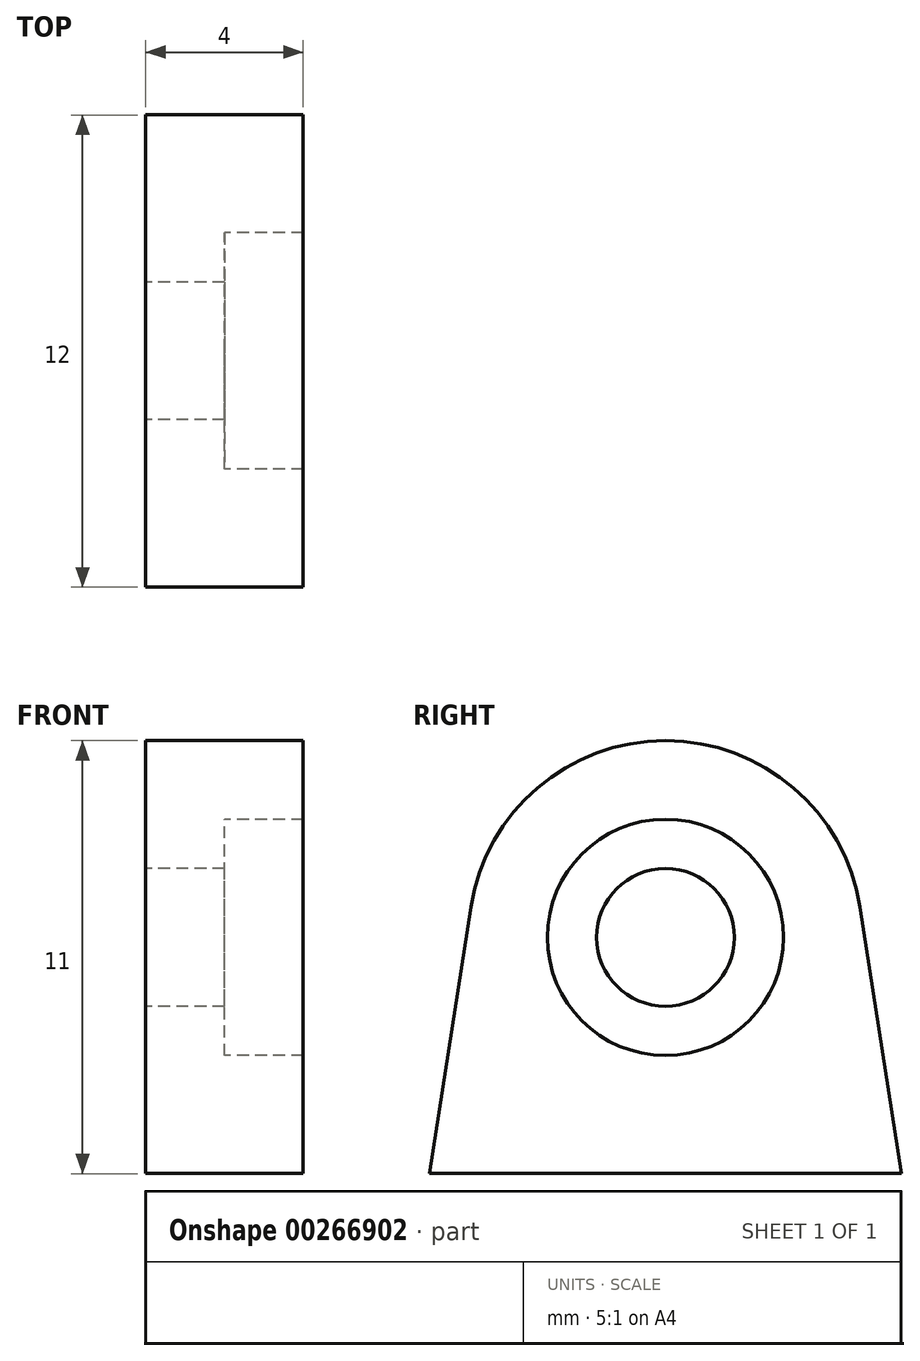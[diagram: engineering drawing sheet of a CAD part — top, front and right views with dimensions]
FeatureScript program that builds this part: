
annotation { "Feature Type Name" : "Feature", "Feature Type Description" : "" }
export const myFeature = defineFeature(function(context is Context, id is Id, definition is map)
    precondition{}
    {
        {
            var Q0;
            Q0=qCreatedBy(makeId("Right.planeOp"),FACE);
            var sketch = newSketch(context, id + "F0", { "sketchPlane" : qUnion([Q0])});
            skCircle(sketch, "E0", {"center": v(-26.77, 32.62) * mm, "radius": 5 * mm});
            skLineSegment(sketch, "E1", {"start": v(-32.77, 26.62) * mm, "end": v(-20.77, 26.62) * mm});
            skLineSegment(sketch, "E2", {"start": v(-31.7, 33.4) * mm, "end": v(-32.77, 26.62) * mm});
            skLineSegment(sketch, "E3", {"start": v(-21.83, 33.4) * mm, "end": v(-20.77, 26.62) * mm});
            skCircle(sketch, "E4", {"center": v(-26.77, 32.62) * mm, "radius": 1.75 * mm});
            skCircle(sketch, "E5", {"center": v(-26.77, 32.62) * mm, "radius": 3 * mm});
            skSolve(sketch);
        }
        {
            var Q0;
            Q0 = qSketchRegion(id + "F0", true);
            extrude(context, id + "F1", {"entities" : qUnion([Q0]), "depth" : 4 * mm});
        }
        {
            var Q0;
            Q0=makeQuery(id+"F0.imprint","IMPRINT",FACE,{"disambiguationData":[TD([[makeQuery(id+"F0.imprint","IMPRINT",EDGE,{"derivedFrom":sQuery(id+"F0.wireOp",EDGE,"E4")}),-1.0]])]});
            extrude(context, id + "F2", {"entities" : qUnion([Q0]), "operationType" : NewBodyOperationType.ADD, "depth" : 2 * mm});
        }
    });
